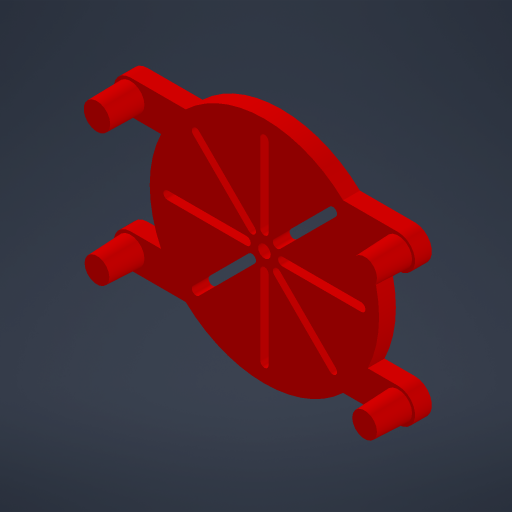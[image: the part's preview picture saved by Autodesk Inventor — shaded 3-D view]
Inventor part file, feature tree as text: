
AUTODESK INVENTOR PART (.ipt)
format: ipt  version: 2023.4 (Build 274418000, 418)  size: 306,176 bytes
history: native  units: mm
features: chamfer x4, other x3, extrude x2, reference x2
ambient origin geometry x8: Origin, YZ Plane, XZ Plane, XY Plane, X Axis, Y Axis, Z Axis, Center Point
bodies: Solid1 (feature_tree)
feature tree (11):
  extrude  "Extrusion2"  Depth=2.5mm TaperAngle=0.0deg
  extrude  "Extrusion3"  Depth=5.0mm TaperAngle=0.0deg
  chamfer  "Chamfer1"  Distance=5.0mm
  chamfer  "Chamfer2"  Distance=5.0mm
  chamfer  "Chamfer3"  Distance=5.0mm
  chamfer  "Chamfer4"  Distance=5.0mm
  reference  "Reference14"
  reference  "Reference15"
  other  "<path>\Projects\Project Protocube\Protocube\CAD, STL, OBJ Files\1 CAD\Cube 1x1 V5.iam"
  other  "Cube 1x1 V5.iam"
  other  "Cube 1x1 Bottom V5 Closed:1"
note: 1 file-system path scrubbed to <path> (originals preserved in map.json)
